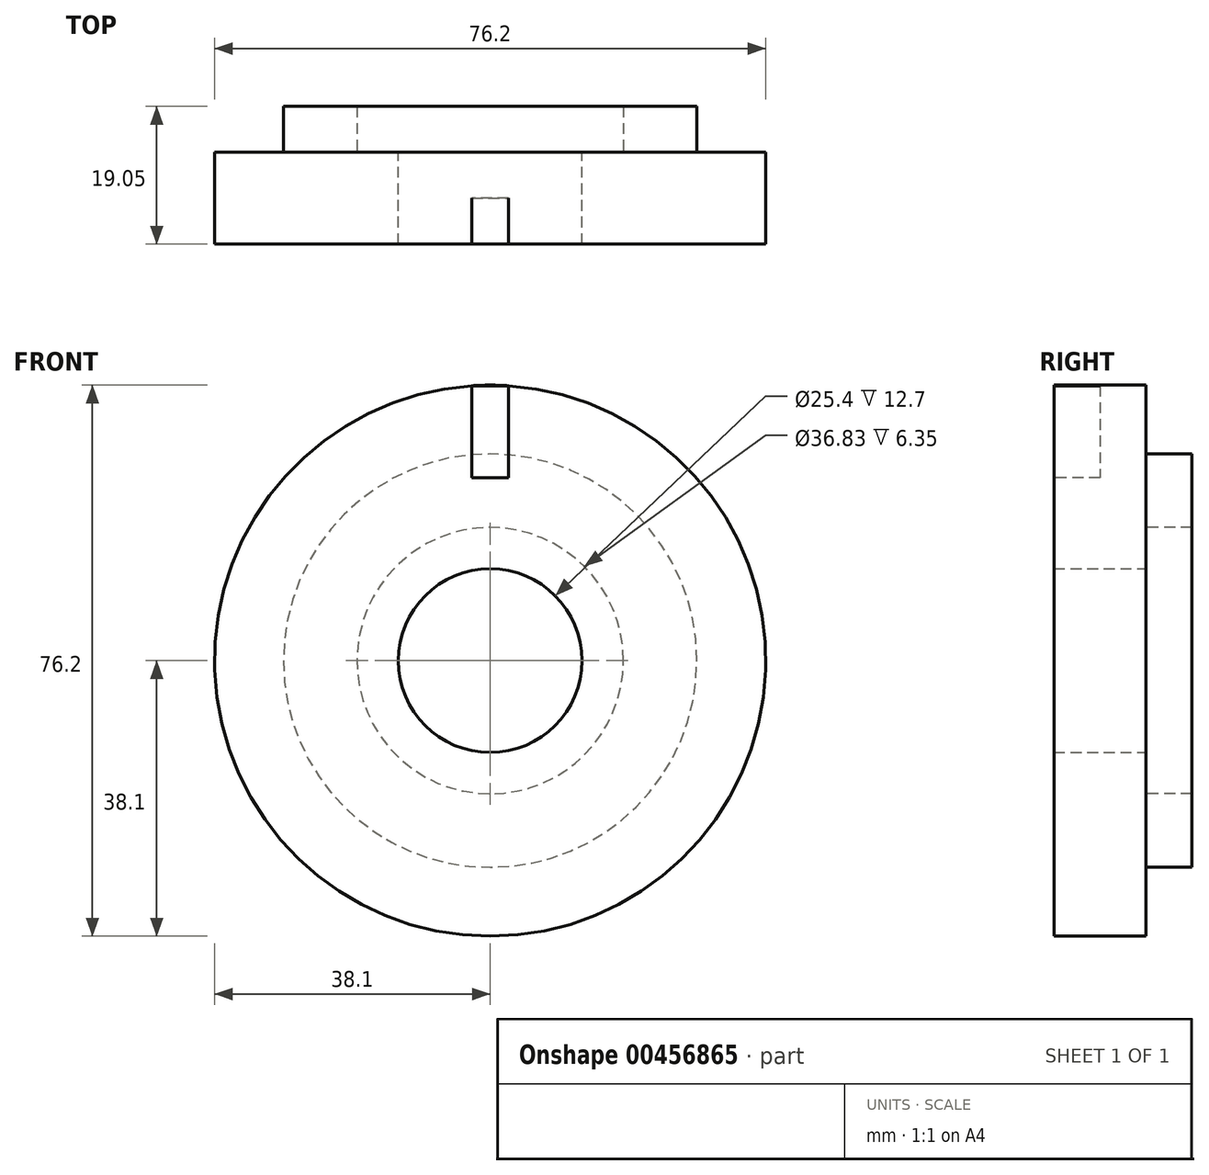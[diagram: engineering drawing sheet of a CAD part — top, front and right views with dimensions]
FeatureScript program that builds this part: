
annotation { "Feature Type Name" : "Feature", "Feature Type Description" : "" }
export const myFeature = defineFeature(function(context is Context, id is Id, definition is map)
    precondition{}
    {
        {
            var Q0;
            Q0=qCreatedBy(makeId("Front.planeOp"),FACE);
            var sketch = newSketch(context, id + "F0", { "sketchPlane" : qUnion([Q0])});
            skCircle(sketch, "E0", {"center": v(0, 0) * mm, "radius": 38.1 * mm});
            skCircle(sketch, "E1", {"center": v(0, 0) * mm, "radius": 12.7 * mm});
            skCircle(sketch, "E2", {"center": v(0, 0) * mm, "radius": 34.93 * mm, "construction": true});
            skPoint(sketch, "E3", {"position": v(0, 34.93) * mm});
            skPoint(sketch, "E4", {"position": v(-34.93, 0) * mm});
            skPoint(sketch, "E5", {"position": v(0, -34.92) * mm});
            skPoint(sketch, "E6", {"position": v(34.93, 0) * mm});
            skSolve(sketch);
        }
        {
            var Q0;
            Q0=qSketchRegion(id+"F0",true);
            extrude(context, id + "F1", {"entities" : qUnion([Q0]), "depth" : 12.7 * mm});
        }
        {
            var Q0;
            Q0=makeQuery(id+"F1.opExtrude","CAP_FACE",FACE,{"disambiguationData":[OSD([sQuery(id+"F0.wireOp",EDGE,"E0"),sQuery(id+"F0.wireOp",EDGE,"E1")])],"isStart":true});
            var sketch = newSketch(context, id + "F2", { "sketchPlane" : qUnion([Q0])});
            skCircle(sketch, "E7", {"center": v(0, 0) * mm, "radius": 18.41 * mm});
            skCircle(sketch, "E8", {"center": v(0, 0) * mm, "radius": 28.58 * mm});
            skSolve(sketch);
        }
        {
            var Q0;
            Q0=makeQuery(id+"F2.imprint","IMPRINT",FACE,{"disambiguationData":[TD([[makeQuery(id+"F2.imprint","IMPRINT",EDGE,{"derivedFrom":sQuery(id+"F2.wireOp",EDGE,"E7")}),-1.0]])]});
            extrude(context, id + "F3", {"entities" : qUnion([Q0]), "operationType" : NewBodyOperationType.ADD, "depth" : 6.35 * mm});
        }
        {
            var Q0;
            Q0=makeQuery(id+"F1.opExtrude","CAP_FACE",FACE,{"disambiguationData":[OSD([sQuery(id+"F0.wireOp",EDGE,"E0"),sQuery(id+"F0.wireOp",EDGE,"E1")])],"isStart":false});
            var sketch = newSketch(context, id + "F4", { "sketchPlane" : qUnion([Q0])});
            skLineSegment(sketch, "E9.bottom", {"start": v(-2.54, 38.02) * mm, "end": v(2.54, 38.02) * mm});
            skLineSegment(sketch, "E9.top", {"start": v(-2.54, 25.32) * mm, "end": v(2.54, 25.32) * mm});
            skLineSegment(sketch, "E9.left", {"start": v(-2.54, 38.02) * mm, "end": v(-2.54, 25.32) * mm});
            skLineSegment(sketch, "E9.right", {"start": v(2.54, 38.02) * mm, "end": v(2.54, 25.32) * mm});
            skSolve(sketch);
        }
        {
            var Q0;
            Q0=qSketchRegion(id+"F4",true);
            extrude(context, id + "F5", {"entities" : qUnion([Q0]), "operationType" : NewBodyOperationType.REMOVE, "oppositeDirection" : true, "depth" : 6.35 * mm});
        }
    });
